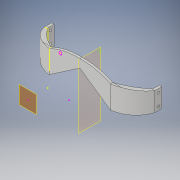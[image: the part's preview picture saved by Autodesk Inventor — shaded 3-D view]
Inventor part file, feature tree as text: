
AUTODESK INVENTOR PART (.ipt)
format: ipt  version: 2019 (Build 230136000, 136)  size: 352,256 bytes
history: native  units: mm
features: sketch x12, extrude x8, other x7, projected_geometry x3, mirror x2, loft x1
ambient origin geometry x8: Origin, YZ Plane, XZ Plane, XY Plane, X Axis, Y Axis, Z Axis, Center Point
bodies: Body1 (feature_tree)
feature tree (33):
  other  "Bryła1"
  sketch  "Szkic1"
  other  "Płaszczyzna konstrukcyjna8"
  sketch  "Szkic2"
  other  "Płaszczyzna konstrukcyjna2"
  extrude  "Wyciągnięcie proste1"  Depth=4.0mm
  sketch  "Szkic4"
  sketch  "Szkic5"
  other  "Płaszczyzna konstrukcyjna9"
  extrude  "Wyciągnięcie proste2"  Depth=8.9mm TaperAngle=0.0deg
  sketch  "Szkic20"
  sketch  "Szkic21"
  extrude  "Wyciągnięcie proste3"  Depth=3.0mm
  other  "Płaszczyzna konstrukcyjna10"
  extrude  "Wyciągnięcie proste4"  Depth=3.0mm
  extrude  "Wyciągnięcie proste5"  Depth=24.0mm
  extrude  "Wyciągnięcie proste6"  Depth=3.0mm TaperAngle=0.0deg
  loft  "Wyciągnięcie złożone2"
  extrude  "Wyciągnięcie proste7"  Depth=100.0mm TaperAngle=0.0deg
  mirror  "Odbij1"
  extrude  "Wyciągnięcie proste9"  Depth=250.0mm TaperAngle=0.0deg
  mirror  "Odbij2"
  sketch  "Szkic3"
  projected_geometry  "Pętla rzutowana1"
  projected_geometry  "Pętla rzutowana2"
  sketch  "Szkic19"
  projected_geometry  "Pętla rzutowana3"
  sketch  "Szkic23"
  sketch  "Szkic24"
  sketch  "Szkic25"
  other  "Krawędzie3"
  other  "Krawędzie4"
  sketch  "Szkic26"
